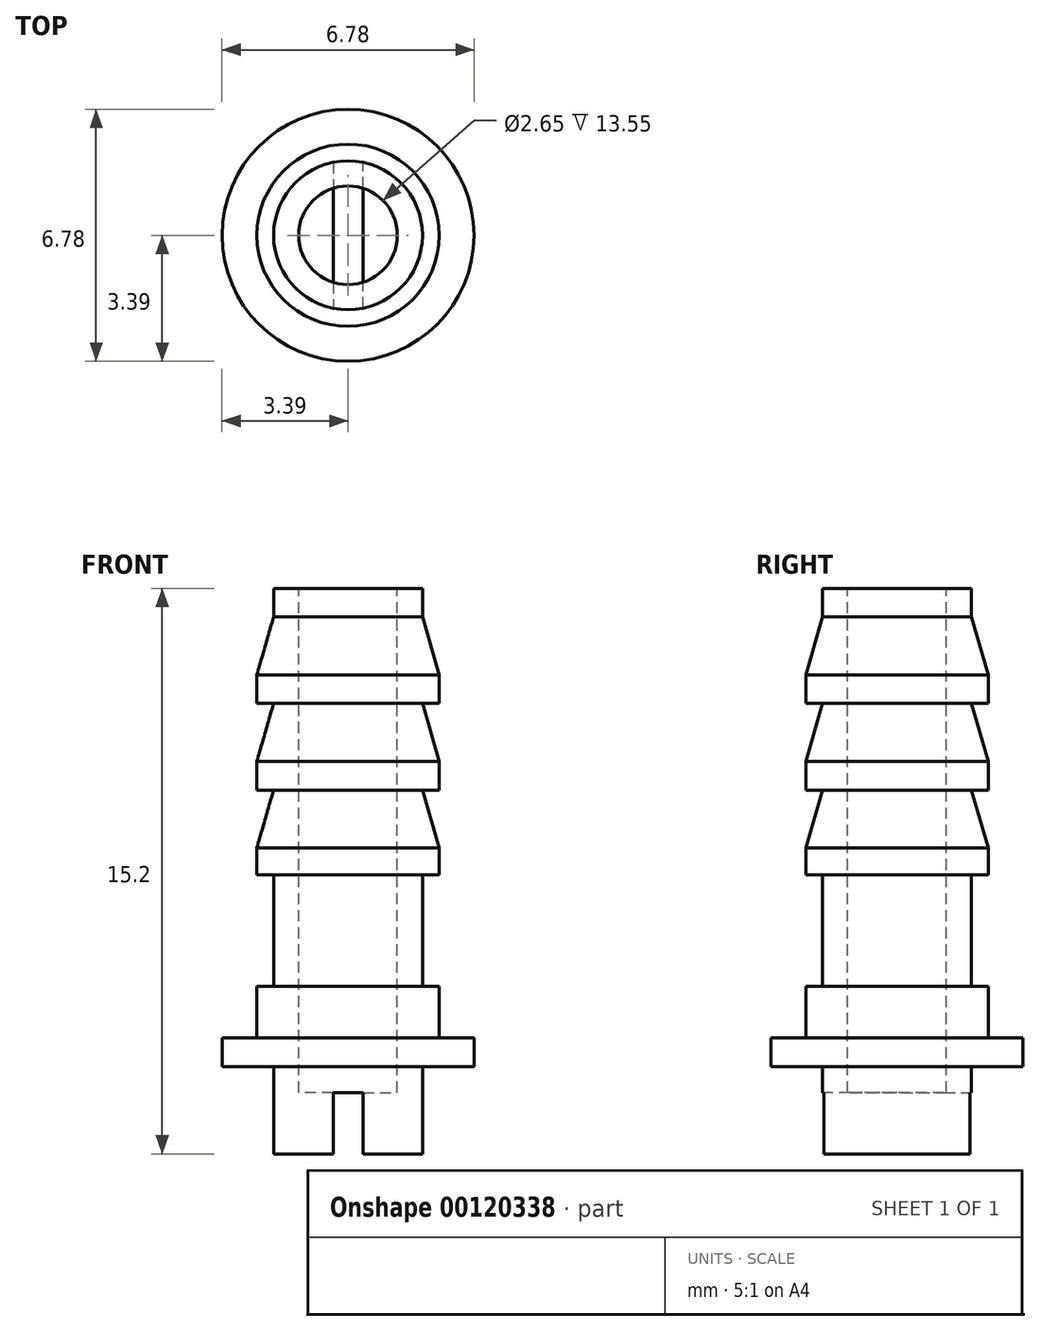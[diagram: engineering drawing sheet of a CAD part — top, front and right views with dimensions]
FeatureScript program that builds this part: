
annotation { "Feature Type Name" : "Feature", "Feature Type Description" : "" }
export const myFeature = defineFeature(function(context is Context, id is Id, definition is map)
    precondition{}
    {
        {
            var Q0;
            Q0=qCreatedBy(makeId("Top.planeOp"),FACE);
            var sketch = newSketch(context, id + "F0", { "sketchPlane" : qUnion([Q0])});
            skCircle(sketch, "E0", {"center": v(0, 0) * mm, "radius": 3.39 * mm});
            skSolve(sketch);
        }
        {
            var Q0;
            Q0 = qSketchRegion(id + "F0", true);
            extrude(context, id + "F1", {"entities" : qUnion([Q0]), "depth" : 15.2 * mm});
        }
        {
            var Q0;
            Q0=makeQuery(id+"F1.opExtrude","CAP_FACE",FACE,{"disambiguationData":[OSD([sQuery(id+"F0.wireOp",EDGE,"E0")])],"isStart":true});
            var sketch = newSketch(context, id + "F2", { "sketchPlane" : qUnion([Q0])});
            skCircle(sketch, "E1", {"center": v(0, 0) * mm, "radius": 2 * mm});
            skLineSegment(sketch, "E2", {"start": v(-0.4, -1.96) * mm, "end": v(-0.4, 1.96) * mm});
            skLineSegment(sketch, "E3", {"start": v(0.4, 1.96) * mm, "end": v(0.4, -1.96) * mm});
            skPoint(sketch, "E4", {"position": v(0.4, 0) * mm});
            skPoint(sketch, "E5", {"position": v(-0.4, 0) * mm});
            skLineSegment(sketch, "E6", {"start": v(0, 4.1) * mm, "end": v(0, -4.43) * mm, "construction": true});
            skSolve(sketch);
        }
        {
            var Q0;
            Q0=makeQuery(id+"F2.imprint","IMPRINT",FACE,{"disambiguationData":[TD([[makeQuery(id+"F2.imprint","IMPRINT",EDGE,{"derivedFrom":sQuery(id+"F2.wireOp",EDGE,"E1")}),-1.0]])]});
            extrude(context, id + "F3", {"entities" : qUnion([Q0]), "operationType" : NewBodyOperationType.REMOVE, "oppositeDirection" : true, "depth" : 2.35 * mm});
        }
        {
            var Q0;
            {var subQ0=sQuery(id+"F2.wireOp",EDGE,"E2");Q0=makeQuery(id+"F2.imprint","IMPRINT",FACE,{"disambiguationData":[TD([[makeQuery(id+"F2.imprint","IMPRINT",EDGE,{"derivedFrom":subQ0}),-1.0]])]});}
            extrude(context, id + "F4", {"entities" : qUnion([Q0]), "operationType" : NewBodyOperationType.REMOVE, "oppositeDirection" : true, "depth" : 1.65 * mm});
        }
        {
            var Q0;
            Q0=makeQuery(id+"F3.boolean.opBoolean","COPY",FACE,{"derivedFrom":makeQuery(id+"F3.opExtrude","CAP_FACE",FACE,{"disambiguationData":[OSD([sQuery(id+"F0.wireOp",EDGE,"E0"),sQuery(id+"F2.wireOp",EDGE,"E1")])],"isStart":false})});
            cPlane(context, id + "F5", {"entities" : qUnion([Q0]), "cplaneType" : CPlaneType.OFFSET, "offset" : 0.77 * mm, "oppositeDirection" : true, "width" : 150 * mm, "height" : 150 * mm});
        }
        {
            var Q0;
            Q0=makeQuery(id+"F1.opExtrude","CAP_FACE",FACE,{"disambiguationData":[OSD([sQuery(id+"F0.wireOp",EDGE,"E0")])],"isStart":false});
            var sketch = newSketch(context, id + "F6", { "sketchPlane" : qUnion([Q0])});
            skCircle(sketch, "E7", {"center": v(0, 0) * mm, "radius": 2.45 * mm});
            skSolve(sketch);
        }
        {
            var Q0;
            Q0=makeQuery(id+"F6.imprint","IMPRINT",FACE,{"disambiguationData":[TD([[makeQuery(id+"F6.imprint","IMPRINT",EDGE,{"derivedFrom":sQuery(id+"F6.wireOp",EDGE,"E7")}),-1.0]])]});
            var Q1;
            Q1=qCreatedBy(id+"F5.planeOp",FACE);
            extrude(context, id + "F7", {"entities" : qUnion([Q0]), "operationType" : NewBodyOperationType.REMOVE, "endBound" : BoundingType.UP_TO_SURFACE, "oppositeDirection" : true, "endBoundEntityFace" : qUnion([Q1]), "depth" : 25 * mm});
        }
        {
            var Q0;
            Q0=makeQuery(id+"F1.opExtrude","CAP_FACE",FACE,{"disambiguationData":[OSD([sQuery(id+"F0.wireOp",EDGE,"E0")])],"isStart":false});
            cPlane(context, id + "F8", {"entities" : qUnion([Q0]), "cplaneType" : CPlaneType.OFFSET, "offset" : 10.7 * mm, "oppositeDirection" : true, "width" : 150 * mm, "height" : 150 * mm});
        }
        {
            var Q0;
            Q0=qCreatedBy(id+"F8.planeOp",FACE);
            var sketch = newSketch(context, id + "F9", { "sketchPlane" : qUnion([Q0])});
            skPoint(sketch, "E8.0", {"position": v(0, 0) * mm});
            skCircle(sketch, "E9", {"center": v(0, 0) * mm, "radius": 2 * mm});
            skCircle(sketch, "E10.0", {"center": v(0, 0) * mm, "radius": 3.39 * mm});
            skSolve(sketch);
        }
        {
            var Q0;
            Q0=makeQuery(id+"F9.imprint","IMPRINT",FACE,{"disambiguationData":[TD([[makeQuery(id+"F9.imprint","IMPRINT",EDGE,{"derivedFrom":sQuery(id+"F9.wireOp",EDGE,"E9")}),-1.0]])]});
            extrude(context, id + "F10", {"entities" : qUnion([Q0]), "operationType" : NewBodyOperationType.REMOVE, "depth" : 3 * mm});
        }
        {
            var Q0;
            Q0=makeQuery(id+"F1.opExtrude","CAP_FACE",FACE,{"disambiguationData":[OSD([sQuery(id+"F0.wireOp",EDGE,"E0")])],"isStart":false});
            var sketch = newSketch(context, id + "F11", { "sketchPlane" : qUnion([Q0])});
            skCircle(sketch, "E11", {"center": v(0, 0) * mm, "radius": 2 * mm});
            skSolve(sketch);
        }
        {
            var Q0;
            Q0=makeQuery(id+"F11.imprint","IMPRINT",FACE,{"disambiguationData":[TD([[makeQuery(id+"F11.imprint","IMPRINT",EDGE,{"derivedFrom":sQuery(id+"F11.wireOp",EDGE,"E11")}),-1.0]])]});
            extrude(context, id + "F12", {"entities" : qUnion([Q0]), "operationType" : NewBodyOperationType.REMOVE, "oppositeDirection" : true, "depth" : 0.77 * mm});
        }
        {
            var Q0;
            Q0=makeQuery(id+"F12.boolean.opBoolean","COPY",FACE,{"derivedFrom":makeQuery(id+"F12.opExtrude","CAP_FACE",FACE,{"disambiguationData":[OSD([sQuery(id+"F6.wireOp",EDGE,"E7"),sQuery(id+"F11.wireOp",EDGE,"E11")])],"isStart":false})});
            cPlane(context, id + "F13", {"entities" : qUnion([Q0]), "cplaneType" : CPlaneType.OFFSET, "offset" : 1.55 * mm, "oppositeDirection" : true, "width" : 150 * mm, "height" : 150 * mm});
        }
        {
            var Q0;
            Q0=qCreatedBy(id+"F13.planeOp",FACE);
            cPlane(context, id + "F14", {"entities" : qUnion([Q0]), "cplaneType" : CPlaneType.OFFSET, "offset" : 0.77 * mm, "oppositeDirection" : true, "width" : 150 * mm, "height" : 150 * mm});
        }
        {
            var Q0;
            Q0=qCreatedBy(id+"F14.planeOp",FACE);
            cPlane(context, id + "F15", {"entities" : qUnion([Q0]), "cplaneType" : CPlaneType.OFFSET, "offset" : 1.55 * mm, "oppositeDirection" : true, "width" : 150 * mm, "height" : 150 * mm});
        }
        {
            var Q0;
            Q0=qCreatedBy(id+"F15.planeOp",FACE);
            cPlane(context, id + "F16", {"entities" : qUnion([Q0]), "cplaneType" : CPlaneType.OFFSET, "offset" : 0.77 * mm, "oppositeDirection" : true, "width" : 150 * mm, "height" : 150 * mm});
        }
        {
            var Q0;
            Q0=qCreatedBy(id+"F16.planeOp",FACE);
            cPlane(context, id + "F17", {"entities" : qUnion([Q0]), "cplaneType" : CPlaneType.OFFSET, "offset" : 1.55 * mm, "oppositeDirection" : true, "width" : 150 * mm, "height" : 150 * mm});
        }
        {
            var Q0;
            Q0=makeQuery(id+"F12.boolean.opBoolean","COPY",FACE,{"derivedFrom":makeQuery(id+"F12.opExtrude","CAP_FACE",FACE,{"disambiguationData":[OSD([sQuery(id+"F6.wireOp",EDGE,"E7"),sQuery(id+"F11.wireOp",EDGE,"E11")])],"isStart":false})});
            var sketch = newSketch(context, id + "F18", { "sketchPlane" : qUnion([Q0])});
            skCircle(sketch, "E12.0", {"center": v(0, 0) * mm, "radius": 2 * mm});
            skSolve(sketch);
        }
        {
            var Q0;
            Q0=qCreatedBy(id+"F13.planeOp",FACE);
            var sketch = newSketch(context, id + "F19", { "sketchPlane" : qUnion([Q0])});
            skCircle(sketch, "E13.0", {"center": v(0, 0) * mm, "radius": 2.45 * mm});
            skSolve(sketch);
        }
        {
            var Q0;
            Q0=qCreatedBy(makeId("Front.planeOp"),FACE);
            var sketch = newSketch(context, id + "F20", { "sketchPlane" : qUnion([Q0])});
            skLineSegment(sketch, "E14.0", {"start": v(-2, 14.43) * mm, "end": v(2, 14.43) * mm});
            skLineSegment(sketch, "E15.0", {"start": v(-2.45, 12.88) * mm, "end": v(2.45, 12.88) * mm});
            skLineSegment(sketch, "E16", {"start": v(-2, 14.43) * mm, "end": v(-2.45, 12.88) * mm});
            skLineSegment(sketch, "E17", {"start": v(-2, 12.88) * mm, "end": v(-2, 14.43) * mm});
            skLineSegment(sketch, "E18", {"start": v(-2.45, 14.43) * mm, "end": v(-2, 14.43) * mm});
            skLineSegment(sketch, "E19", {"start": v(-2.45, 14.43) * mm, "end": v(-2.45, 12.88) * mm});
            skSolve(sketch);
        }
        {
            var Q0;
            Q0=qCreatedBy(id+"F14.planeOp",FACE);
            var sketch = newSketch(context, id + "F21", { "sketchPlane" : qUnion([Q0])});
            skCircle(sketch, "E20.0", {"center": v(0, 0) * mm, "radius": 2 * mm});
            skSolve(sketch);
        }
        {
            var Q0;
            Q0=qCreatedBy(id+"F15.planeOp",FACE);
            var sketch = newSketch(context, id + "F22", { "sketchPlane" : qUnion([Q0])});
            skCircle(sketch, "E21.0", {"center": v(0, 0) * mm, "radius": 2.45 * mm});
            skSolve(sketch);
        }
        {
            var Q0;
            Q0=qCreatedBy(makeId("Front.planeOp"),FACE);
            var sketch = newSketch(context, id + "F23", { "sketchPlane" : qUnion([Q0])});
            skLineSegment(sketch, "E22.0", {"start": v(-2, 12.1) * mm, "end": v(2, 12.1) * mm});
            skLineSegment(sketch, "E23.0", {"start": v(-2.45, 10.55) * mm, "end": v(2.45, 10.55) * mm});
            skLineSegment(sketch, "E24", {"start": v(-2, 12.1) * mm, "end": v(-2.45, 10.55) * mm});
            skLineSegment(sketch, "E25", {"start": v(-2, 12.1) * mm, "end": v(-2, 10.55) * mm});
            skLineSegment(sketch, "E26", {"start": v(-2.45, 12.1) * mm, "end": v(-2.45, 10.55) * mm});
            skLineSegment(sketch, "E27", {"start": v(-2.45, 12.1) * mm, "end": v(-2, 12.1) * mm});
            skSolve(sketch);
        }
        {
            var Q0;
            Q0=qCreatedBy(id+"F16.planeOp",FACE);
            var sketch = newSketch(context, id + "F24", { "sketchPlane" : qUnion([Q0])});
            skCircle(sketch, "E28.0", {"center": v(0, 0) * mm, "radius": 2 * mm});
            skSolve(sketch);
        }
        {
            var Q0;
            Q0=qCreatedBy(id+"F17.planeOp",FACE);
            var sketch = newSketch(context, id + "F25", { "sketchPlane" : qUnion([Q0])});
            skCircle(sketch, "E29.0", {"center": v(0, 0) * mm, "radius": 2.45 * mm});
            skSolve(sketch);
        }
        {
            var Q0;
            Q0=qCreatedBy(makeId("Front.planeOp"),FACE);
            var sketch = newSketch(context, id + "F26", { "sketchPlane" : qUnion([Q0])});
            skLineSegment(sketch, "E30.0", {"start": v(-2, 9.78) * mm, "end": v(2, 9.78) * mm});
            skLineSegment(sketch, "E31.0", {"start": v(-2.45, 8.22) * mm, "end": v(2.45, 8.22) * mm});
            skLineSegment(sketch, "E32", {"start": v(-2, 9.78) * mm, "end": v(-2.45, 8.22) * mm});
            skLineSegment(sketch, "E33", {"start": v(-2, 9.78) * mm, "end": v(-2, 8.22) * mm});
            skLineSegment(sketch, "E34", {"start": v(-2, 9.78) * mm, "end": v(-2.45, 9.78) * mm});
            skLineSegment(sketch, "E35", {"start": v(-2.45, 9.78) * mm, "end": v(-2.45, 8.22) * mm});
            skSolve(sketch);
        }
        {
            var Q0;
            Q0=qCreatedBy(makeId("Front.planeOp"),FACE);
            var sketch = newSketch(context, id + "F27", { "sketchPlane" : qUnion([Q0])});
            skLineSegment(sketch, "E36.0", {"start": v(-2.45, 10.55) * mm, "end": v(2.45, 10.55) * mm, "construction": true});
            skLineSegment(sketch, "E37", {"start": v(0, 15.36) * mm, "end": v(0, 5.1) * mm, "construction": true});
            skPoint(sketch, "E37.startSnap0", {"position": v(0, 10.55) * mm});
            skSolve(sketch);
        }
        {
            var Q0;
            Q0=makeQuery(id+"F20.imprint","IMPRINT",FACE,{"disambiguationData":[TD([[makeQuery(id+"F20.imprint","IMPRINT",EDGE,{"derivedFrom":sQuery(id+"F20.wireOp",EDGE,"E16")}),-1.0]])]});
            var Q1;
            Q1=sQuery(id+"F27.wireOp",EDGE,"E37");
            revolve(context, id + "F28", {"operationType" : NewBodyOperationType.REMOVE, "entities" : qUnion([Q0]), "axis" : qUnion([Q1]), "revolveType" : RevolveType.FULL, "oppositeDirection" : true});
        }
        {
            var Q0;
            Q0=makeQuery(id+"F23.imprint","IMPRINT",FACE,{"disambiguationData":[TD([[makeQuery(id+"F23.imprint","IMPRINT",EDGE,{"derivedFrom":sQuery(id+"F23.wireOp",EDGE,"E24")}),-1.0]])]});
            var Q1;
            Q1=sQuery(id+"F27.wireOp",EDGE,"E37");
            revolve(context, id + "F29", {"operationType" : NewBodyOperationType.REMOVE, "entities" : qUnion([Q0]), "axis" : qUnion([Q1]), "revolveType" : RevolveType.FULL, "oppositeDirection" : true});
        }
        {
            var Q0;
            Q0=makeQuery(id+"F26.imprint","IMPRINT",FACE,{"disambiguationData":[TD([[makeQuery(id+"F26.imprint","IMPRINT",EDGE,{"derivedFrom":sQuery(id+"F26.wireOp",EDGE,"E32")}),-1.0]])]});
            var Q1;
            Q1=sQuery(id+"F27.wireOp",EDGE,"E37");
            revolve(context, id + "F30", {"operationType" : NewBodyOperationType.REMOVE, "entities" : qUnion([Q0]), "axis" : qUnion([Q1]), "revolveType" : RevolveType.FULL, "oppositeDirection" : true});
        }
        {
            var Q0;
            Q0=makeQuery(id+"F1.opExtrude","CAP_FACE",FACE,{"disambiguationData":[OSD([sQuery(id+"F0.wireOp",EDGE,"E0")])],"isStart":false});
            var sketch = newSketch(context, id + "F31", { "sketchPlane" : qUnion([Q0])});
            skCircle(sketch, "E38", {"center": v(0, 0) * mm, "radius": 1.32 * mm});
            skSolve(sketch);
        }
        {
            var Q0;
            Q0=makeQuery(id+"F31.imprint","IMPRINT",FACE,{"disambiguationData":[TD([[makeQuery(id+"F31.imprint","IMPRINT",EDGE,{"derivedFrom":sQuery(id+"F31.wireOp",EDGE,"E38")}),1.0]])]});
            var Q1;
            Q1=makeQuery(id+"F4.boolean.opBoolean","COPY",FACE,{"derivedFrom":makeQuery(id+"F4.opExtrude","CAP_FACE",FACE,{"disambiguationData":[OSD([sQuery(id+"F2.wireOp",EDGE,"E1"),sQuery(id+"F2.wireOp",EDGE,"E2"),sQuery(id+"F2.wireOp",EDGE,"E3")])],"isStart":false})});
            extrude(context, id + "F32", {"entities" : qUnion([Q0]), "operationType" : NewBodyOperationType.REMOVE, "endBound" : BoundingType.UP_TO_SURFACE, "oppositeDirection" : true, "endBoundEntityFace" : qUnion([Q1]), "depth" : 25 * mm});
        }
    });
